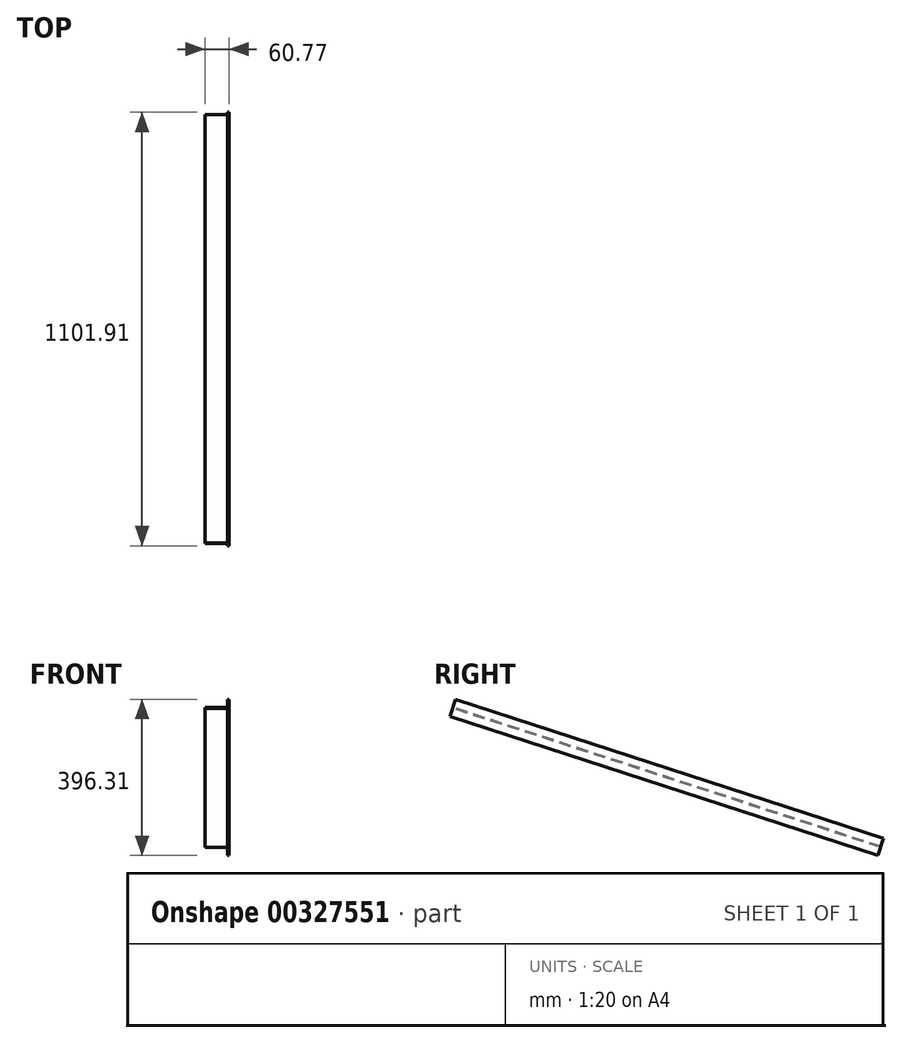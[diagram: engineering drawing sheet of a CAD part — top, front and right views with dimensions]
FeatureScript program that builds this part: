
annotation { "Feature Type Name" : "Feature", "Feature Type Description" : "" }
export const myFeature = defineFeature(function(context is Context, id is Id, definition is map)
    precondition{}
    {
        {
            var Q0;
            Q0=qCreatedBy(makeId("Right.planeOp"),FACE);
            var sketch = newSketch(context, id + "F0", { "sketchPlane" : qUnion([Q0])});
            skLineSegment(sketch, "E0", {"start": v(0, 0) * mm, "end": v(-1088, 0) * mm});
            skLineSegment(sketch, "E1", {"start": v(0, 0) * mm, "end": v(-1088, 353.51) * mm});
            skLineSegment(sketch, "E2", {"start": v(-1088, 0) * mm, "end": v(-1088, 353.51) * mm});
            skLineSegment(sketch, "E3", {"start": v(0, 0) * mm, "end": v(13.9, 42.8) * mm});
            skLineSegment(sketch, "E4", {"start": v(13.9, 42.8) * mm, "end": v(-1074.1, 396.31) * mm});
            skLineSegment(sketch, "E5", {"start": v(-1088, 353.51) * mm, "end": v(-1074.1, 396.31) * mm});
            skLineSegment(sketch, "E6", {"start": v(-1081.05, 374.91) * mm, "end": v(6.95, 21.4) * mm});
            skLineSegment(sketch, "E7", {"start": v(-1081.51, 373.48) * mm, "end": v(6.49, 19.97) * mm});
            skLineSegment(sketch, "E8", {"start": v(7.42, 22.83) * mm, "end": v(-1080.58, 376.34) * mm});
            skSolve(sketch);
        }
        {
            var Q0;
            {var subQ0=sQuery(id+"F0.wireOp",EDGE,"E4");Q0=makeQuery(id+"F0.imprint","IMPRINT",FACE,{"disambiguationData":[TD([[makeQuery(id+"F0.imprint","IMPRINT",EDGE,{"derivedFrom":subQ0}),1.0]])]});}
            var Q1;
            {var subQ0=sQuery(id+"F0.wireOp",EDGE,"E1");Q1=makeQuery(id+"F0.imprint","IMPRINT",FACE,{"disambiguationData":[TD([[makeQuery(id+"F0.imprint","IMPRINT",EDGE,{"derivedFrom":subQ0}),-1.0]])]});}
            var Q2;
            {var subQ0=sQuery(id+"F0.wireOp",EDGE,"E6");Q2=makeQuery(id+"F0.imprint","IMPRINT",FACE,{"disambiguationData":[TD([[makeQuery(id+"F0.imprint","IMPRINT",EDGE,{"derivedFrom":subQ0}),-1.0]])]});}
            var Q3;
            {var subQ0=sQuery(id+"F0.wireOp",EDGE,"E6");Q3=makeQuery(id+"F0.imprint","IMPRINT",FACE,{"disambiguationData":[TD([[makeQuery(id+"F0.imprint","IMPRINT",EDGE,{"derivedFrom":subQ0}),1.0]])]});}
            extrude(context, id + "F1", {"entities" : qUnion([Q0, Q1, Q2, Q3]), "oppositeDirection" : true, "depth" : 3 * mm});
        }
        {
            var Q0;
            {var subQ0=sQuery(id+"F0.wireOp",EDGE,"E5");Q0=makeQuery(id+"FOA5rmWozsO9xZ6_1.boolean.opBoolean","MERGE",FACE,{"derivedFrom":[makeQuery(id+"F1.opExtrude","SWEPT_FACE",FACE,{"disambiguationData":[OSD([subQ0])]}),makeQuery(id+"FOA5rmWozsO9xZ6_1.opExtrude","SWEPT_FACE",FACE,{"disambiguationData":[OSD([subQ0])]})]});}
            var sketch = newSketch(context, id + "F2", { "sketchPlane" : qUnion([Q0])});
            skLineSegment(sketch, "E9", {"start": v(0, 22.5) * mm, "end": v(-3, 22.5) * mm});
            skLineSegment(sketch, "E10", {"start": v(-57.32, 22.5) * mm, "end": v(-3, 22.5) * mm});
            skLineSegment(sketch, "E11.top", {"start": v(-60.77, 21) * mm, "end": v(-3, 21) * mm});
            skLineSegment(sketch, "E11.right", {"start": v(-3, 22.5) * mm, "end": v(-3, 21) * mm});
            skLineSegment(sketch, "E12.bottom", {"start": v(-60.77, 22.5) * mm, "end": v(-3, 22.5) * mm});
            skLineSegment(sketch, "E12.top", {"start": v(-60.77, 24) * mm, "end": v(-3, 24) * mm});
            skLineSegment(sketch, "E12.right", {"start": v(-3, 22.5) * mm, "end": v(-3, 24) * mm});
            skLineSegment(sketch, "E13", {"start": v(-3, 22.5) * mm, "end": v(-6.45, -3.79) * mm});
            skLineSegment(sketch, "E14", {"start": v(-6.45, -3.79) * mm, "end": v(-60.77, -3.79) * mm});
            skLineSegment(sketch, "E15", {"start": v(-60.77, -3.79) * mm, "end": v(-3, 22.5) * mm});
            skLineSegment(sketch, "E16", {"start": v(-60.77, -3.79) * mm, "end": v(-57.32, 22.5) * mm});
            skLineSegment(sketch, "E17", {"start": v(-60.77, -3.79) * mm, "end": v(-60.77, 21) * mm});
            skLineSegment(sketch, "E18", {"start": v(-60.77, 22.5) * mm, "end": v(-60.77, 24) * mm});
            skLineSegment(sketch, "E19", {"start": v(-60.77, 21) * mm, "end": v(-60.77, 22.5) * mm});
            skSolve(sketch);
        }
        {
            var Q0;
            {var subQ0=sQuery(id+"F2.wireOp",EDGE,"E12.right");Q0=makeQuery(id+"F2.imprint","IMPRINT",FACE,{"disambiguationData":[TD([[makeQuery(id+"F2.imprint","IMPRINT",EDGE,{"derivedFrom":subQ0}),1.0]])]});}
            var Q1;
            {var subQ5=sQuery(id+"F2.wireOp",EDGE,"rIjuAr39-bKG2-aq7s-xHkO-0OLbPZ9XOXza");Q1=makeQuery(id+"F2.imprint","IMPRINT",FACE,{"disambiguationData":[TD([[makeQuery(id+"F2.imprint","IMPRINT",EDGE,{"derivedFrom":subQ5}),1.0]])]});}
            var Q2;
            {var subQ0=sQuery(id+"F2.wireOp",EDGE,"E11.right");Q2=makeQuery(id+"F2.imprint","IMPRINT",FACE,{"disambiguationData":[TD([[makeQuery(id+"F2.imprint","IMPRINT",EDGE,{"derivedFrom":subQ0}),1.0]])]});}
            var Q3;
            {var subQ1=sQuery(id+"F2.wireOp",EDGE,"E12.bottom");var subQ7=makeQuery(id+"F2.imprint","IMPRINT",VERTEX,{"derivedFrom":subQ1});Q3=makeQuery(id+"F2.imprint","IMPRINT",FACE,{"disambiguationData":[TD([[makeQuery(id+"F2.imprint","IMPRINT",EDGE,{"disambiguationData":[TD([[subQ7,1.0]])],"derivedFrom":subQ1}),-1.0]])]});}
            var Q4;
            {var subQ0=sQuery(id+"F2.wireOp",EDGE,"E13");var subQ1=sQuery(id+"F2.wireOp",EDGE,"E11.top");var subQ2=makeQuery(id+"F2.imprint","INTERSECT",VERTEX,{"derivedFrom":[subQ1,subQ0]});Q4=makeQuery(id+"F2.imprint","IMPRINT",FACE,{"disambiguationData":[TD([[makeQuery(id+"F2.imprint","IMPRINT",EDGE,{"disambiguationData":[TD([[subQ2,1.0]])],"derivedFrom":subQ1}),1.0]])]});}
            var Q5;
            {var subQ0=sQuery(id+"F2.wireOp",EDGE,"E16");var subQ1=sQuery(id+"F2.wireOp",EDGE,"E11.top");var subQ2=makeQuery(id+"F2.imprint","INTERSECT",VERTEX,{"derivedFrom":[subQ1,subQ0]});Q5=makeQuery(id+"F2.imprint","IMPRINT",FACE,{"disambiguationData":[TD([[makeQuery(id+"F2.imprint","IMPRINT",EDGE,{"disambiguationData":[TD([[subQ2,-1.0]])],"derivedFrom":subQ1}),1.0]])]});}
            var Q6;
            {var subQ0=sQuery(id+"F2.wireOp",EDGE,"E19");Q6=makeQuery(id+"F2.imprint","IMPRINT",FACE,{"disambiguationData":[TD([[makeQuery(id+"F2.imprint","IMPRINT",EDGE,{"derivedFrom":subQ0}),-1.0]])]});}
            var Q7;
            Q7=makeQuery(id+"F1.opExtrude","SWEPT_FACE",FACE,{"disambiguationData":[OSD([sQuery(id+"F0.wireOp",EDGE,"E3")])]});
            extrude(context, id + "F3", {"entities" : qUnion([Q0, Q1, Q2, Q3, Q4, Q5, Q6]), "operationType" : NewBodyOperationType.ADD, "endBound" : BoundingType.UP_TO_SURFACE, "oppositeDirection" : true, "endBoundEntityFace" : qUnion([Q7]), "depth" : 25 * mm});
        }
    });
